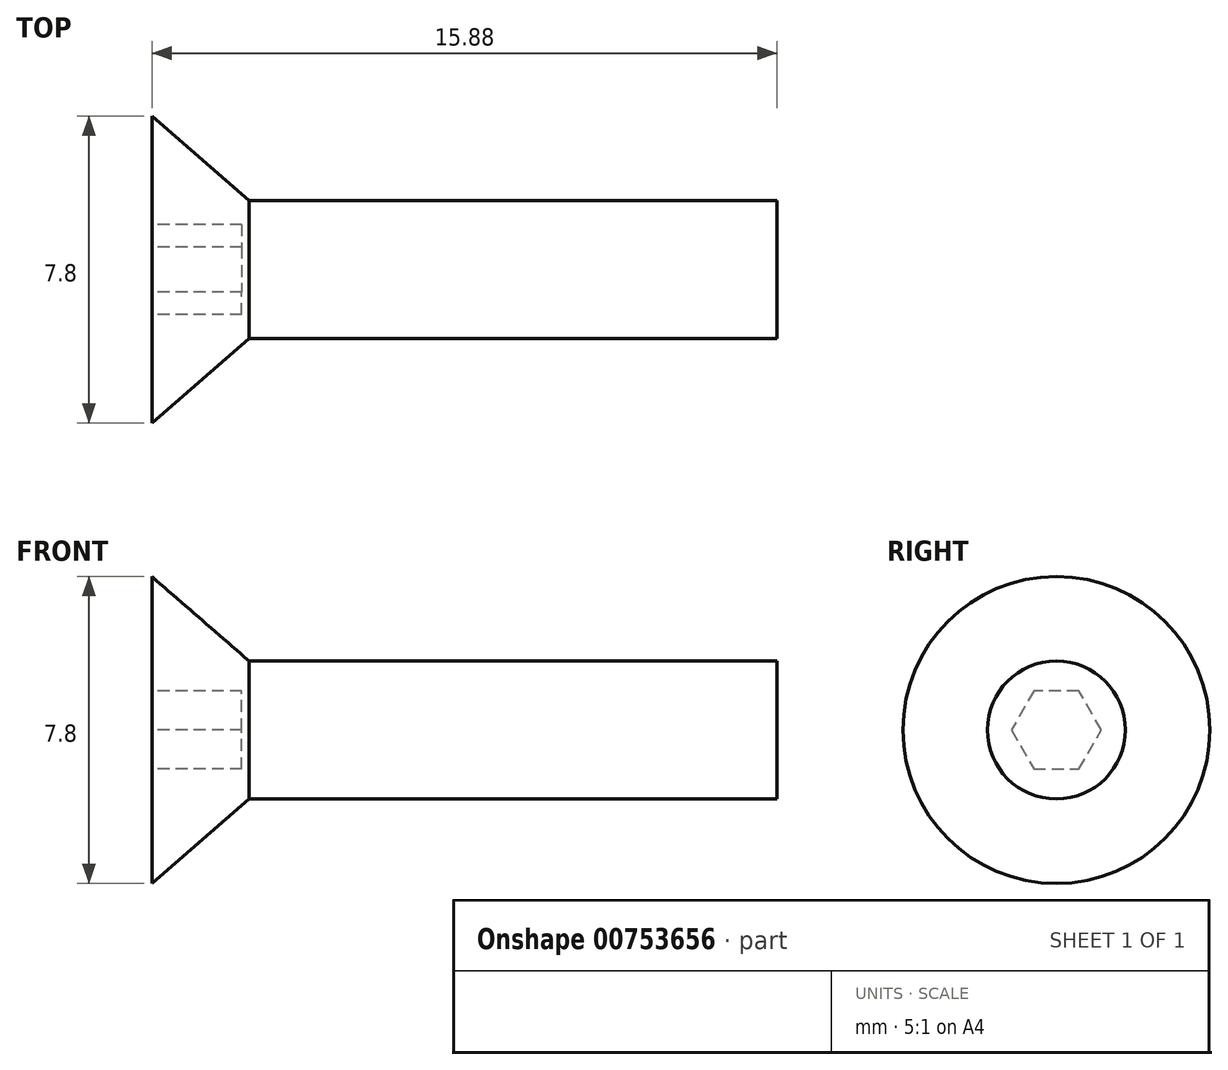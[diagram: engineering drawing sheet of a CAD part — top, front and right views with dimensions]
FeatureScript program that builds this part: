
annotation { "Feature Type Name" : "Feature", "Feature Type Description" : "" }
export const myFeature = defineFeature(function(context is Context, id is Id, definition is map)
    precondition{}
    {
        {
            var Q0;
            Q0=qCreatedBy(makeId("Top.planeOp"),FACE);
            var sketch = newSketch(context, id + "F0", { "sketchPlane" : qUnion([Q0])});
            skLineSegment(sketch, "E0", {"start": v(15.88, -1.75) * mm, "end": v(2.47, -1.75) * mm});
            skLineSegment(sketch, "E1", {"start": v(2.47, -1.75) * mm, "end": v(0, -3.9) * mm});
            skLineSegment(sketch, "E2", {"start": v(0, -3.9) * mm, "end": v(0, 0) * mm});
            skLineSegment(sketch, "E3", {"start": v(15.88, -1.75) * mm, "end": v(15.88, 0) * mm});
            skLineSegment(sketch, "E4", {"start": v(15.88, 0) * mm, "end": v(0, 0) * mm});
            skSolve(sketch);
        }
        {
            var Q0;
            Q0=qCreatedBy(makeId("Top.planeOp"),FACE);
            var sketch = newSketch(context, id + "F1", { "sketchPlane" : qUnion([Q0])});
            skLineSegment(sketch, "E5", {"start": v(-2.4, 0) * mm, "end": v(12.33, 0) * mm, "construction": true});
            skSolve(sketch);
        }
        {
            var Q0;
            Q0=makeQuery(id+"F0.imprint","IMPRINT",FACE,{"disambiguationData":[TD([[makeQuery(id+"F0.imprint","IMPRINT",EDGE,{"derivedFrom":sQuery(id+"F0.wireOp",EDGE,"shhdlBdX-mxSS-FPoy-qKl1-WTqEborUyv4W")}),-1.0]])]});
            var Q1;
            Q1=makeQuery(id+"F0.imprint","IMPRINT",FACE,{"disambiguationData":[TD([[makeQuery(id+"F0.imprint","IMPRINT",EDGE,{"derivedFrom":sQuery(id+"F0.wireOp",EDGE,"E0")}),-1.0]])]});
            var Q2;
            Q2=sQuery(id+"F1.wireOp",EDGE,"E5");
            revolve(context, id + "F2", {"surfaceOperationType" : NewSurfaceOperationType.NEW, "entities" : qUnion([Q0, Q1]), "axis" : qUnion([Q2]), "revolveType" : RevolveType.FULL});
        }
        {
            var Q0;
            Q0=makeQuery(id+"F2.opRevolve","SWEPT_FACE",FACE,{"disambiguationData":[OSD([sQuery(id+"F0.wireOp",EDGE,"E2")])]});
            var sketch = newSketch(context, id + "F3", { "sketchPlane" : qUnion([Q0])});
            skCircle(sketch, "E6.cCircle", {"center": v(0, 0) * mm, "radius": 1 * mm, "construction": true});
            skLineSegment(sketch, "E6.0", {"start": v(-0.57, 1) * mm, "end": v(0.57, 1) * mm});
            skLineSegment(sketch, "E6.1", {"start": v(0.57, 1) * mm, "end": v(1.15, 0) * mm});
            skLineSegment(sketch, "E6.2", {"start": v(1.15, 0) * mm, "end": v(0.57, -1) * mm});
            skLineSegment(sketch, "E6.3", {"start": v(0.57, -1) * mm, "end": v(-0.57, -1) * mm});
            skLineSegment(sketch, "E6.4", {"start": v(-0.57, -1) * mm, "end": v(-1.15, 0) * mm});
            skLineSegment(sketch, "E6.5", {"start": v(-1.15, 0) * mm, "end": v(-0.57, 1) * mm});
            skPoint(sketch, "E6.0.midPoint", {"position": v(0, 1) * mm});
            skSolve(sketch);
        }
        {
            var Q0;
            Q0=makeQuery(id+"F3.imprint","IMPRINT",FACE,{"disambiguationData":[TD([[makeQuery(id+"F3.imprint","IMPRINT",EDGE,{"derivedFrom":sQuery(id+"F3.wireOp",EDGE,"E6.0")}),-1.0]])]});
            extrude(context, id + "F4", {"entities" : qUnion([Q0]), "operationType" : NewBodyOperationType.REMOVE, "oppositeDirection" : true, "depth" : 2.3 * mm, "offsetDistance" : 25.4 * mm});
        }
    });
